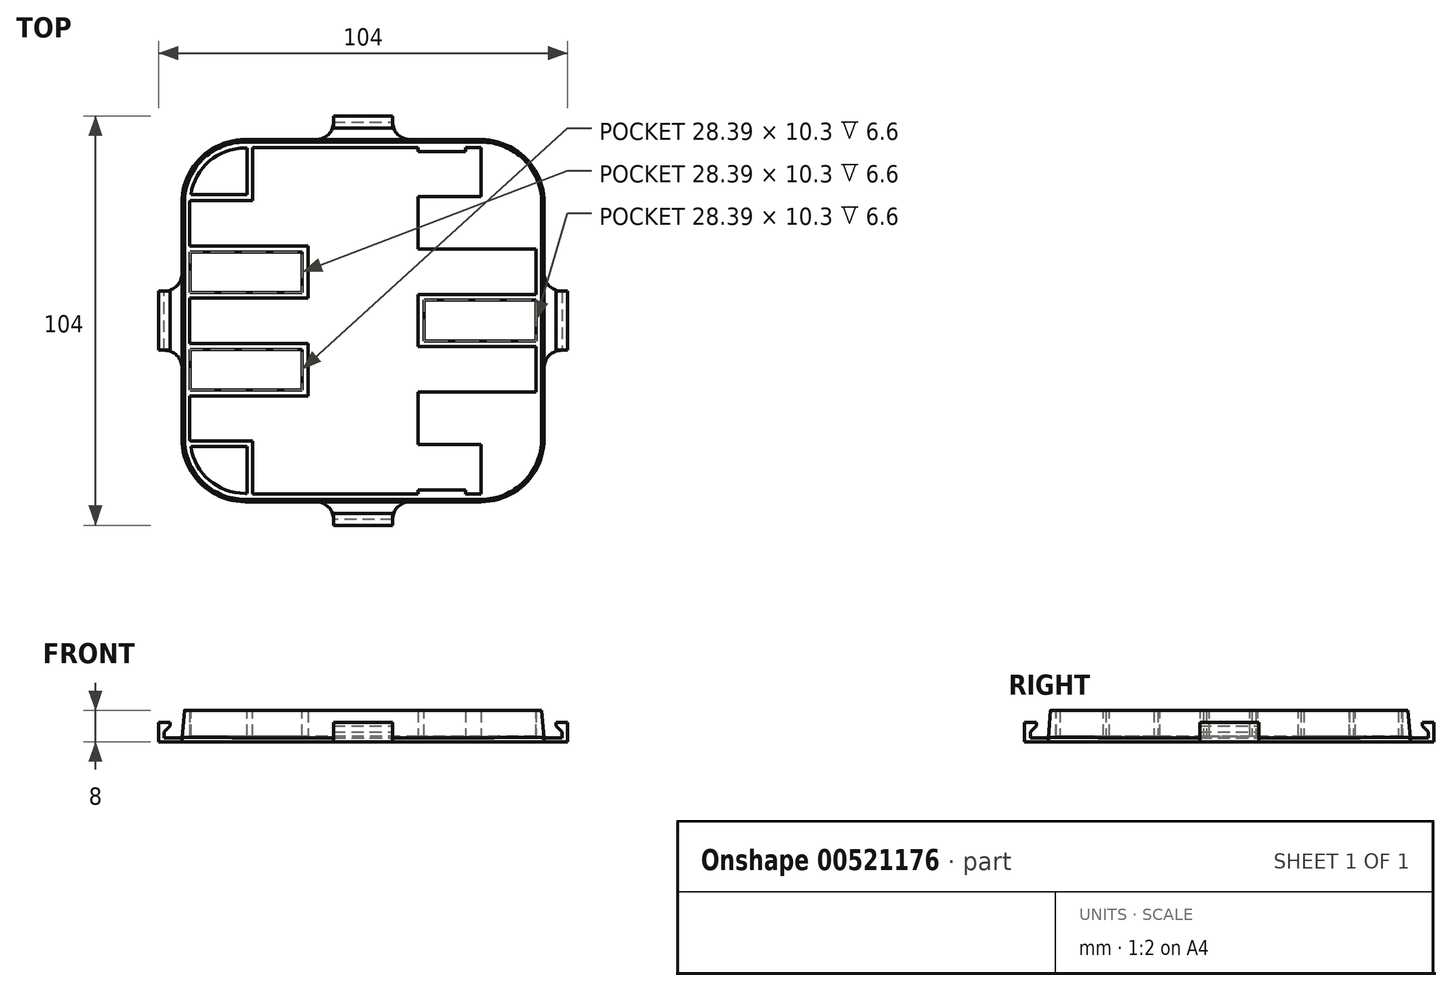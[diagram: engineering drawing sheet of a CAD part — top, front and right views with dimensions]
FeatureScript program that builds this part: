
annotation { "Feature Type Name" : "Feature", "Feature Type Description" : "" }
export const myFeature = defineFeature(function(context is Context, id is Id, definition is map)
    precondition{}
    {
        {
            var Q0;
            Q0=qCreatedBy(makeId("Top.planeOp"),FACE);
            var sketch = newSketch(context, id + "F0", { "sketchPlane" : qUnion([Q0])});
            skPoint(sketch, "E0.middle", {"position": v(0, 0) * mm});
            skPoint(sketch, "E1.visualSharp", {"position": v(40, 40) * mm});
            skArc(sketch, "E1.filletArc", {"start": v(52, 30) * mm, "mid": v(45.56, 45.56) * mm, "end": v(30, 52) * mm});
            skPoint(sketch, "E2.visualSharp", {"position": v(40, -40) * mm});
            skArc(sketch, "E2.filletArc", {"start": v(30, -52) * mm, "mid": v(45.56, -45.56) * mm, "end": v(52, -30) * mm});
            skPoint(sketch, "E3.visualSharp", {"position": v(-40, -40) * mm});
            skArc(sketch, "E3.filletArc", {"start": v(-52, -30) * mm, "mid": v(-45.56, -45.56) * mm, "end": v(-30, -52) * mm});
            skPoint(sketch, "E4.visualSharp", {"position": v(-40, 40) * mm});
            skArc(sketch, "E4.filletArc", {"start": v(-30, 52) * mm, "mid": v(-45.56, 45.56) * mm, "end": v(-52, 30) * mm});
            skLineSegment(sketch, "E5", {"start": v(52, 30) * mm, "end": v(52, 0) * mm});
            skLineSegment(sketch, "E6", {"start": v(52, 0) * mm, "end": v(52, -30) * mm});
            skLineSegment(sketch, "E7", {"start": v(30, 52) * mm, "end": v(0, 52) * mm});
            skLineSegment(sketch, "E8", {"start": v(0, 52) * mm, "end": v(-30, 52) * mm});
            skLineSegment(sketch, "E9", {"start": v(-52, 30) * mm, "end": v(-52, 0) * mm});
            skLineSegment(sketch, "E10", {"start": v(-52, 0) * mm, "end": v(-52, -30) * mm});
            skLineSegment(sketch, "E11", {"start": v(-30, -52) * mm, "end": v(0, -52) * mm});
            skLineSegment(sketch, "E12", {"start": v(0, -52) * mm, "end": v(30, -52) * mm});
            skSolve(sketch);
        }
        {
            var Q0;
            Q0=qCreatedBy(makeId("Front.planeOp"),FACE);
            var sketch = newSketch(context, id + "F1", { "sketchPlane" : qUnion([Q0])});
            skLineSegment(sketch, "E13", {"start": v(44, 0) * mm, "end": v(52, 0) * mm});
            skLineSegment(sketch, "E14", {"start": v(52, 0) * mm, "end": v(52, 1) * mm});
            skLineSegment(sketch, "E15", {"start": v(46, 1) * mm, "end": v(45.39, 8) * mm});
            skLineSegment(sketch, "E16", {"start": v(45.39, 8) * mm, "end": v(44, 8) * mm});
            skLineSegment(sketch, "E17", {"start": v(44, 8) * mm, "end": v(44, 0) * mm});
            skPoint(sketch, "E18.orphan", {"position": v(0, 8) * mm});
            skPoint(sketch, "E19.orphan", {"position": v(0, 0) * mm});
            skLineSegment(sketch, "E20", {"start": v(50.5, 1) * mm, "end": v(46, 1) * mm});
            skLineSegment(sketch, "E21", {"start": v(52, 1) * mm, "end": v(52, 5) * mm});
            skLineSegment(sketch, "E22", {"start": v(52, 5) * mm, "end": v(49, 5) * mm});
            skLineSegment(sketch, "E23", {"start": v(49, 5) * mm, "end": v(49, 4) * mm});
            skLineSegment(sketch, "E24", {"start": v(49, 4) * mm, "end": v(50.5, 2.5) * mm});
            skLineSegment(sketch, "E25", {"start": v(50.5, 2.5) * mm, "end": v(50.5, 1) * mm});
            skSolve(sketch);
        }
        {
            var Q0;
            Q0 = qSketchRegion(id + "F1", true);
            var Q1;
            Q1 = qConstructionFilter(qBodyType(qCreatedBy(id + "F0" ,EDGE), BodyType.WIRE), ConstructionObject.NO);
            sweep(context, id + "F2", {"profiles" : qUnion([Q0]), "path" : qUnion([Q1])});
        }
        {
            var Q0;
            Q0=qCreatedBy(makeId("Top.planeOp"),FACE);
            var sketch = newSketch(context, id + "F3", { "sketchPlane" : qUnion([Q0])});
            skLineSegment(sketch, "E26.0", {"start": v(-30, -44) * mm, "end": v(30, -44) * mm});
            skArc(sketch, "E27.0", {"start": v(-44, -30) * mm, "mid": v(-39.9, -39.9) * mm, "end": v(-30, -44) * mm});
            skLineSegment(sketch, "E28.0", {"start": v(-44, 30) * mm, "end": v(-44, -30) * mm});
            skArc(sketch, "E29.0", {"start": v(30, -44) * mm, "mid": v(39.9, -39.9) * mm, "end": v(44, -30) * mm});
            skLineSegment(sketch, "E30.0", {"start": v(44, -30) * mm, "end": v(44, 30) * mm});
            skArc(sketch, "E31.0", {"start": v(44, 30) * mm, "mid": v(39.9, 39.9) * mm, "end": v(30, 44) * mm});
            skLineSegment(sketch, "E32.0", {"start": v(30, 44) * mm, "end": v(-30, 44) * mm});
            skArc(sketch, "E33.0", {"start": v(-30, 44) * mm, "mid": v(-39.9, 39.9) * mm, "end": v(-44, 30) * mm});
            skSolve(sketch);
        }
        {
            var Q0;
            Q0 = qSketchRegion(id + "F3", true);
            extrude(context, id + "F4", {"entities" : qUnion([Q0]), "operationType" : NewBodyOperationType.ADD, "depth" : 1.4 * mm, "offsetDistance" : 25 * mm});
        }
        {
            var Q0;
            Q0=makeQuery(id+"F4.opExtrude","CAP_FACE",FACE,{"disambiguationData":[OSD([sQuery(id+"F3.wireOp",EDGE,"E26.0"),sQuery(id+"F3.wireOp",EDGE,"E27.0"),sQuery(id+"F3.wireOp",EDGE,"E28.0"),sQuery(id+"F3.wireOp",EDGE,"E29.0"),sQuery(id+"F3.wireOp",EDGE,"E30.0"),sQuery(id+"F3.wireOp",EDGE,"E31.0"),sQuery(id+"F3.wireOp",EDGE,"E32.0"),sQuery(id+"F3.wireOp",EDGE,"E33.0"),sQuery(id+"F3.wireOp",EDGE,"Zldg7baT-O6LS-5cXX-1kl8-0yIzSKLbcUxf")])],"isStart":false});
            var sketch = newSketch(context, id + "F5", { "sketchPlane" : qUnion([Q0])});
            skLineSegment(sketch, "E34.bottom", {"start": v(44, 31.5) * mm, "end": v(14, 31.5) * mm});
            skLineSegment(sketch, "E34.top", {"start": v(44, 18.2) * mm, "end": v(14, 18.2) * mm});
            skLineSegment(sketch, "E34.left", {"start": v(44, 31.5) * mm, "end": v(44, 18.2) * mm});
            skLineSegment(sketch, "E34.right", {"start": v(14, 31.5) * mm, "end": v(14, 18.2) * mm});
            skLineSegment(sketch, "E35.bottom", {"start": v(14, 44) * mm, "end": v(26, 44) * mm});
            skLineSegment(sketch, "E35.top", {"start": v(14, 43) * mm, "end": v(26, 43) * mm});
            skLineSegment(sketch, "E35.left", {"start": v(14, 44) * mm, "end": v(14, 43) * mm});
            skLineSegment(sketch, "E35.right", {"start": v(26, 44) * mm, "end": v(26, 43) * mm});
            skLineSegment(sketch, "E36.bottom", {"start": v(44, 6.7) * mm, "end": v(14, 6.7) * mm});
            skLineSegment(sketch, "E36.top", {"start": v(44, -6.6) * mm, "end": v(14, -6.6) * mm});
            skLineSegment(sketch, "E36.left", {"start": v(44, 6.7) * mm, "end": v(44, -6.6) * mm});
            skLineSegment(sketch, "E36.right", {"start": v(14, 6.7) * mm, "end": v(14, -6.6) * mm});
            skLineSegment(sketch, "E37.bottom", {"start": v(44, -18.1) * mm, "end": v(14, -18.1) * mm});
            skLineSegment(sketch, "E37.top", {"start": v(44, -31.4) * mm, "end": v(14, -31.4) * mm});
            skLineSegment(sketch, "E37.left", {"start": v(44, -18.1) * mm, "end": v(44, -31.4) * mm});
            skLineSegment(sketch, "E37.right", {"start": v(14, -18.1) * mm, "end": v(14, -31.4) * mm});
            skLineSegment(sketch, "E38.bottom", {"start": v(14, -44) * mm, "end": v(26, -44) * mm});
            skLineSegment(sketch, "E38.top", {"start": v(14, -43) * mm, "end": v(26, -43) * mm});
            skLineSegment(sketch, "E38.left", {"start": v(14, -44) * mm, "end": v(14, -43) * mm});
            skLineSegment(sketch, "E38.right", {"start": v(26, -44) * mm, "end": v(26, -43) * mm});
            skLineSegment(sketch, "E39.bottom", {"start": v(-44, 30.5) * mm, "end": v(-14, 30.5) * mm});
            skLineSegment(sketch, "E39.top", {"start": v(-30, 44) * mm, "end": v(-14, 44) * mm});
            skLineSegment(sketch, "E39.left", {"start": v(-44, 30) * mm, "end": v(-44, 30.5) * mm});
            skLineSegment(sketch, "E39.right", {"start": v(-14, 30.5) * mm, "end": v(-14, 44) * mm});
            skArc(sketch, "E40.0", {"start": v(-30, 44) * mm, "mid": v(-39.9, 39.9) * mm, "end": v(-44, 30) * mm});
            skLineSegment(sketch, "E41.bottom", {"start": v(-14, -44) * mm, "end": v(-30, -44) * mm});
            skLineSegment(sketch, "E41.top", {"start": v(-14, -30.5) * mm, "end": v(-44, -30.5) * mm});
            skLineSegment(sketch, "E41.left", {"start": v(-14, -44) * mm, "end": v(-14, -30.5) * mm});
            skLineSegment(sketch, "E41.right", {"start": v(-44, -30.5) * mm, "end": v(-44, -30) * mm});
            skArc(sketch, "E42.0", {"start": v(-44, -30) * mm, "mid": v(-39.9, -39.9) * mm, "end": v(-30, -44) * mm});
            skLineSegment(sketch, "E43.bottom", {"start": v(-44, 19) * mm, "end": v(-14, 19) * mm});
            skLineSegment(sketch, "E43.top", {"start": v(-44, 5.7) * mm, "end": v(-14, 5.7) * mm});
            skLineSegment(sketch, "E43.left", {"start": v(-44, 19) * mm, "end": v(-44, 5.7) * mm});
            skLineSegment(sketch, "E43.right", {"start": v(-14, 19) * mm, "end": v(-14, 5.7) * mm});
            skLineSegment(sketch, "E44.bottom", {"start": v(-44, -5.8) * mm, "end": v(-14, -5.8) * mm});
            skLineSegment(sketch, "E44.top", {"start": v(-44, -19.1) * mm, "end": v(-14, -19.1) * mm});
            skLineSegment(sketch, "E44.left", {"start": v(-44, -5.8) * mm, "end": v(-44, -19.1) * mm});
            skLineSegment(sketch, "E44.right", {"start": v(-14, -5.8) * mm, "end": v(-14, -19.1) * mm});
            skSolve(sketch);
        }
        {
            var Q0;
            Q0 = qSketchRegion(id + "F5", true);
            var Q1;
            Q1=makeQuery(id+"F2.opSweep","SWEPT_FACE",FACE,{"disambiguationData":[OSD([sQuery(id+"F0.wireOp",EDGE,"E5"),sQuery(id+"F1.wireOp",EDGE,"E16")])]});
            extrude(context, id + "F6", {"entities" : qUnion([Q0]), "operationType" : NewBodyOperationType.ADD, "endBound" : BoundingType.UP_TO_SURFACE, "depth" : 25 * mm, "endBoundEntityFace" : qUnion([Q1]), "offsetDistance" : 25 * mm});
        }
        {
            var Q0;
            Q0=makeQuery(id+"F4.opExtrude","CAP_FACE",FACE,{"disambiguationData":[OSD([sQuery(id+"F3.wireOp",EDGE,"E26.0"),sQuery(id+"F3.wireOp",EDGE,"E27.0"),sQuery(id+"F3.wireOp",EDGE,"E28.0"),sQuery(id+"F3.wireOp",EDGE,"E29.0"),sQuery(id+"F3.wireOp",EDGE,"E30.0"),sQuery(id+"F3.wireOp",EDGE,"E31.0"),sQuery(id+"F3.wireOp",EDGE,"E32.0"),sQuery(id+"F3.wireOp",EDGE,"E33.0")])],"isStart":false});
            var sketch = newSketch(context, id + "F7", { "sketchPlane" : qUnion([Q0])});
            skLineSegment(sketch, "E45", {"start": v(30, 44) * mm, "end": v(30, 31.5) * mm});
            skLineSegment(sketch, "E46", {"start": v(30, 31.5) * mm, "end": v(43.92, 31.5) * mm});
            skLineSegment(sketch, "E47", {"start": v(30, -44) * mm, "end": v(30, -31.4) * mm});
            skLineSegment(sketch, "E48", {"start": v(30, -31.4) * mm, "end": v(43.93, -31.4) * mm});
            skArc(sketch, "E49.0", {"start": v(30, -44) * mm, "mid": v(39.4, -40.38) * mm, "end": v(43.93, -31.4) * mm});
            skSolve(sketch);
        }
        {
            var Q0;
            Q0=makeQuery(id+"F7.imprint","IMPRINT",FACE,{"disambiguationData":[TD([[makeQuery(id+"F7.imprint","IMPRINT",EDGE,{"derivedFrom":sQuery(id+"F7.wireOp",EDGE,"E47")}),-1.0]])]});
            var Q1;
            Q1=makeQuery(id+"F7.imprint","IMPRINT",FACE,{"disambiguationData":[TD([[makeQuery(id+"F7.imprint","IMPRINT",EDGE,{"derivedFrom":sQuery(id+"F7.wireOp",EDGE,"E45")}),1.0]])]});
            var Q2;
            Q2=makeQuery(id+"F6.boolean.opBoolean","MERGE",FACE,{"derivedFrom":[makeQuery(id+"F2.opSweep","SWEPT_FACE",FACE,{"disambiguationData":[OSD([sQuery(id+"F0.wireOp",EDGE,"E5"),sQuery(id+"F1.wireOp",EDGE,"E16")])]}),makeQuery(id+"F6.opExtrude","CAP_FACE",FACE,{"disambiguationData":[OSD([sQuery(id+"F5.wireOp",EDGE,"E34.bottom"),sQuery(id+"F5.wireOp",EDGE,"E34.top"),sQuery(id+"F5.wireOp",EDGE,"E34.left"),sQuery(id+"F5.wireOp",EDGE,"E34.right")])],"isStart":false}),makeQuery(id+"F6.opExtrude","CAP_FACE",FACE,{"disambiguationData":[OSD([sQuery(id+"F5.wireOp",EDGE,"E35.bottom"),sQuery(id+"F5.wireOp",EDGE,"E35.top"),sQuery(id+"F5.wireOp",EDGE,"E35.left"),sQuery(id+"F5.wireOp",EDGE,"E35.right")])],"isStart":false}),makeQuery(id+"F6.opExtrude","CAP_FACE",FACE,{"disambiguationData":[OSD([sQuery(id+"F5.wireOp",EDGE,"E36.bottom"),sQuery(id+"F5.wireOp",EDGE,"E36.top"),sQuery(id+"F5.wireOp",EDGE,"E36.left"),sQuery(id+"F5.wireOp",EDGE,"E36.right")])],"isStart":false}),makeQuery(id+"F6.opExtrude","CAP_FACE",FACE,{"disambiguationData":[OSD([sQuery(id+"F5.wireOp",EDGE,"E37.bottom"),sQuery(id+"F5.wireOp",EDGE,"E37.top"),sQuery(id+"F5.wireOp",EDGE,"E37.left"),sQuery(id+"F5.wireOp",EDGE,"E37.right")])],"isStart":false}),makeQuery(id+"F6.opExtrude","CAP_FACE",FACE,{"disambiguationData":[OSD([sQuery(id+"F5.wireOp",EDGE,"E38.bottom"),sQuery(id+"F5.wireOp",EDGE,"E38.top"),sQuery(id+"F5.wireOp",EDGE,"E38.left"),sQuery(id+"F5.wireOp",EDGE,"E38.right")])],"isStart":false}),makeQuery(id+"F6.opExtrude","CAP_FACE",FACE,{"disambiguationData":[OSD([sQuery(id+"F5.wireOp",EDGE,"E39.bottom"),sQuery(id+"F5.wireOp",EDGE,"E39.top"),sQuery(id+"F5.wireOp",EDGE,"E39.right"),sQuery(id+"F5.wireOp",EDGE,"E40.0")])],"isStart":false}),makeQuery(id+"F6.opExtrude","CAP_FACE",FACE,{"disambiguationData":[OSD([sQuery(id+"F5.wireOp",EDGE,"E41.bottom"),sQuery(id+"F5.wireOp",EDGE,"E41.top"),sQuery(id+"F5.wireOp",EDGE,"E41.left"),sQuery(id+"F5.wireOp",EDGE,"E42.0")])],"isStart":false}),makeQuery(id+"F6.opExtrude","CAP_FACE",FACE,{"disambiguationData":[OSD([sQuery(id+"F5.wireOp",EDGE,"E43.bottom"),sQuery(id+"F5.wireOp",EDGE,"E43.top"),sQuery(id+"F5.wireOp",EDGE,"E43.left"),sQuery(id+"F5.wireOp",EDGE,"E43.right")])],"isStart":false}),makeQuery(id+"F6.opExtrude","CAP_FACE",FACE,{"disambiguationData":[OSD([sQuery(id+"F5.wireOp",EDGE,"E44.bottom"),sQuery(id+"F5.wireOp",EDGE,"E44.top"),sQuery(id+"F5.wireOp",EDGE,"E44.left"),sQuery(id+"F5.wireOp",EDGE,"E44.right")])],"isStart":false})]});
            extrude(context, id + "F8", {"entities" : qUnion([Q0, Q1]), "operationType" : NewBodyOperationType.ADD, "endBound" : BoundingType.UP_TO_SURFACE, "depth" : 25 * mm, "endBoundEntityFace" : qUnion([Q2]), "offsetDistance" : 25 * mm});
        }
        {
            var Q0;
            Q0=makeQuery(id+"F8.boolean.opBoolean","MERGE",FACE,{"derivedFrom":[makeQuery(id+"F6.boolean.opBoolean","MERGE",FACE,{"derivedFrom":[makeQuery(id+"F2.opSweep","SWEPT_FACE",FACE,{"disambiguationData":[OSD([sQuery(id+"F0.wireOp",EDGE,"E5"),sQuery(id+"F1.wireOp",EDGE,"E16")])]}),makeQuery(id+"F6.opExtrude","CAP_FACE",FACE,{"disambiguationData":[OSD([sQuery(id+"F5.wireOp",EDGE,"E34.bottom"),sQuery(id+"F5.wireOp",EDGE,"E34.top"),sQuery(id+"F5.wireOp",EDGE,"E34.left"),sQuery(id+"F5.wireOp",EDGE,"E34.right")])],"isStart":false}),makeQuery(id+"F6.opExtrude","CAP_FACE",FACE,{"disambiguationData":[OSD([sQuery(id+"F5.wireOp",EDGE,"E35.bottom"),sQuery(id+"F5.wireOp",EDGE,"E35.top"),sQuery(id+"F5.wireOp",EDGE,"E35.left"),sQuery(id+"F5.wireOp",EDGE,"E35.right")])],"isStart":false}),makeQuery(id+"F6.opExtrude","CAP_FACE",FACE,{"disambiguationData":[OSD([sQuery(id+"F5.wireOp",EDGE,"E36.bottom"),sQuery(id+"F5.wireOp",EDGE,"E36.top"),sQuery(id+"F5.wireOp",EDGE,"E36.left"),sQuery(id+"F5.wireOp",EDGE,"E36.right")])],"isStart":false}),makeQuery(id+"F6.opExtrude","CAP_FACE",FACE,{"disambiguationData":[OSD([sQuery(id+"F5.wireOp",EDGE,"E37.bottom"),sQuery(id+"F5.wireOp",EDGE,"E37.top"),sQuery(id+"F5.wireOp",EDGE,"E37.left"),sQuery(id+"F5.wireOp",EDGE,"E37.right")])],"isStart":false}),makeQuery(id+"F6.opExtrude","CAP_FACE",FACE,{"disambiguationData":[OSD([sQuery(id+"F5.wireOp",EDGE,"E38.bottom"),sQuery(id+"F5.wireOp",EDGE,"E38.top"),sQuery(id+"F5.wireOp",EDGE,"E38.left"),sQuery(id+"F5.wireOp",EDGE,"E38.right")])],"isStart":false}),makeQuery(id+"F6.opExtrude","CAP_FACE",FACE,{"disambiguationData":[OSD([sQuery(id+"F5.wireOp",EDGE,"E39.bottom"),sQuery(id+"F5.wireOp",EDGE,"E39.top"),sQuery(id+"F5.wireOp",EDGE,"E39.right"),sQuery(id+"F5.wireOp",EDGE,"E40.0")])],"isStart":false}),makeQuery(id+"F6.opExtrude","CAP_FACE",FACE,{"disambiguationData":[OSD([sQuery(id+"F5.wireOp",EDGE,"E41.bottom"),sQuery(id+"F5.wireOp",EDGE,"E41.top"),sQuery(id+"F5.wireOp",EDGE,"E41.left"),sQuery(id+"F5.wireOp",EDGE,"E42.0")])],"isStart":false}),makeQuery(id+"F6.opExtrude","CAP_FACE",FACE,{"disambiguationData":[OSD([sQuery(id+"F5.wireOp",EDGE,"E43.bottom"),sQuery(id+"F5.wireOp",EDGE,"E43.top"),sQuery(id+"F5.wireOp",EDGE,"E43.left"),sQuery(id+"F5.wireOp",EDGE,"E43.right")])],"isStart":false}),makeQuery(id+"F6.opExtrude","CAP_FACE",FACE,{"disambiguationData":[OSD([sQuery(id+"F5.wireOp",EDGE,"E44.bottom"),sQuery(id+"F5.wireOp",EDGE,"E44.top"),sQuery(id+"F5.wireOp",EDGE,"E44.left"),sQuery(id+"F5.wireOp",EDGE,"E44.right")])],"isStart":false})]}),makeQuery(id+"F8.opExtrude","CAP_FACE",FACE,{"disambiguationData":[OSD([sQuery(id+"F3.wireOp",EDGE,"E31.0"),sQuery(id+"F7.wireOp",EDGE,"E45"),sQuery(id+"F7.wireOp",EDGE,"E46")])],"isStart":false}),makeQuery(id+"F8.opExtrude","CAP_FACE",FACE,{"disambiguationData":[OSD([sQuery(id+"F7.wireOp",EDGE,"E47"),sQuery(id+"F7.wireOp",EDGE,"E48"),sQuery(id+"F7.wireOp",EDGE,"E49.0")])],"isStart":false})]});
            var sketch = newSketch(context, id + "F9", { "sketchPlane" : qUnion([Q0])});
            skLineSegment(sketch, "E50.bottom", {"start": v(-14, 44) * mm, "end": v(-28, 44) * mm});
            skLineSegment(sketch, "E50.top", {"start": v(-14, 30.5) * mm, "end": v(-28, 30.5) * mm});
            skLineSegment(sketch, "E50.left", {"start": v(-14, 44) * mm, "end": v(-14, 30.5) * mm});
            skLineSegment(sketch, "E50.right", {"start": v(-28, 44) * mm, "end": v(-28, 30.5) * mm});
            skLineSegment(sketch, "E51.bottom", {"start": v(-14, -44) * mm, "end": v(-28, -44) * mm});
            skLineSegment(sketch, "E51.top", {"start": v(-14, -30.5) * mm, "end": v(-28, -30.5) * mm});
            skLineSegment(sketch, "E51.left", {"start": v(-14, -44) * mm, "end": v(-14, -30.5) * mm});
            skLineSegment(sketch, "E51.right", {"start": v(-28, -44) * mm, "end": v(-28, -30.5) * mm});
            skSolve(sketch);
        }
        {
            var Q0;
            Q0=makeQuery(id+"F9.imprint","IMPRINT",FACE,{"disambiguationData":[TD([[makeQuery(id+"F9.imprint","IMPRINT",EDGE,{"derivedFrom":sQuery(id+"F9.wireOp",EDGE,"E50.bottom")}),1.0]])]});
            var Q1;
            Q1=makeQuery(id+"F9.imprint","IMPRINT",FACE,{"disambiguationData":[TD([[makeQuery(id+"F9.imprint","IMPRINT",EDGE,{"derivedFrom":sQuery(id+"F9.wireOp",EDGE,"E51.bottom")}),-1.0]])]});
            var Q2;
            Q2=makeQuery(id+"F4.opExtrude","CAP_FACE",FACE,{"disambiguationData":[OSD([sQuery(id+"F3.wireOp",EDGE,"E26.0"),sQuery(id+"F3.wireOp",EDGE,"E27.0"),sQuery(id+"F3.wireOp",EDGE,"E28.0"),sQuery(id+"F3.wireOp",EDGE,"E29.0"),sQuery(id+"F3.wireOp",EDGE,"E30.0"),sQuery(id+"F3.wireOp",EDGE,"E31.0"),sQuery(id+"F3.wireOp",EDGE,"E32.0"),sQuery(id+"F3.wireOp",EDGE,"E33.0")])],"isStart":false});
            extrude(context, id + "F10", {"entities" : qUnion([Q0, Q1]), "operationType" : NewBodyOperationType.REMOVE, "endBound" : BoundingType.UP_TO_SURFACE, "oppositeDirection" : true, "depth" : 25 * mm, "endBoundEntityFace" : qUnion([Q2]), "offsetDistance" : 25 * mm});
        }
        {
            var Q0;
            {var subQ0=sQuery(id+"F1.wireOp",EDGE,"E16");var subQ1=sQuery(id+"F0.wireOp",EDGE,"E5");Q0=makeQuery(id+"F6.boolean.opBoolean","MERGE",FACE,{"derivedFrom":[makeQuery(id+"F2.opSweep","SWEPT_FACE",FACE,{"disambiguationData":[OSD([subQ1,subQ0])]}),makeQuery(id+"F6.opExtrude","CAP_FACE",FACE,{"disambiguationData":[OSD([subQ1,subQ0]),OD(0.0)],"isStart":false}),makeQuery(id+"F6.opExtrude","CAP_FACE",FACE,{"disambiguationData":[OSD([subQ1,subQ0]),OD(1.0)],"isStart":false}),makeQuery(id+"F6.opExtrude","CAP_FACE",FACE,{"disambiguationData":[OSD([subQ1,subQ0]),OD(2.0)],"isStart":false}),makeQuery(id+"F6.opExtrude","CAP_FACE",FACE,{"disambiguationData":[OSD([subQ1,subQ0]),OD(3.0)],"isStart":false}),makeQuery(id+"F6.opExtrude","CAP_FACE",FACE,{"disambiguationData":[OSD([subQ1,subQ0]),OD(4.0)],"isStart":false}),makeQuery(id+"F6.opExtrude","CAP_FACE",FACE,{"disambiguationData":[OSD([subQ1,subQ0]),OD(5.0)],"isStart":false}),makeQuery(id+"F6.opExtrude","CAP_FACE",FACE,{"disambiguationData":[OSD([subQ1,subQ0]),OD(6.0)],"isStart":false}),makeQuery(id+"F6.opExtrude","CAP_FACE",FACE,{"disambiguationData":[OSD([subQ1,subQ0]),OD(7.0)],"isStart":false}),makeQuery(id+"F6.opExtrude","CAP_FACE",FACE,{"disambiguationData":[OSD([subQ1,subQ0]),OD(8.0)],"isStart":false})]});}
            var sketch = newSketch(context, id + "F11", { "sketchPlane" : qUnion([Q0])});
            skLineSegment(sketch, "E52.0", {"start": v(-29.5, 32) * mm, "end": v(-29.5, 43.89) * mm});
            skLineSegment(sketch, "E52.1", {"start": v(-43.74, 32) * mm, "end": v(-29.5, 32) * mm});
            skArc(sketch, "E53.1", {"start": v(-30, 43.89) * mm, "mid": v(-39.09, 40.5) * mm, "end": v(-43.74, 32) * mm});
            skLineSegment(sketch, "E53.2", {"start": v(-29.5, 43.89) * mm, "end": v(-30, 43.89) * mm});
            skLineSegment(sketch, "E54.0", {"start": v(-43.89, 7.2) * mm, "end": v(-15.5, 7.2) * mm});
            skLineSegment(sketch, "E54.1", {"start": v(-15.5, 17.5) * mm, "end": v(-15.5, 7.2) * mm});
            skLineSegment(sketch, "E54.2", {"start": v(-43.89, 17.5) * mm, "end": v(-15.5, 17.5) * mm});
            skLineSegment(sketch, "E55", {"start": v(-43.89, 17.5) * mm, "end": v(-43.89, 7.2) * mm});
            skLineSegment(sketch, "E56.0", {"start": v(-43.89, -17.6) * mm, "end": v(-15.5, -17.6) * mm});
            skLineSegment(sketch, "E56.1", {"start": v(-15.5, -7.3) * mm, "end": v(-15.5, -17.6) * mm});
            skLineSegment(sketch, "E56.2", {"start": v(-43.89, -7.3) * mm, "end": v(-15.5, -7.3) * mm});
            skLineSegment(sketch, "E57", {"start": v(-43.89, -7.3) * mm, "end": v(-43.89, -17.6) * mm});
            skLineSegment(sketch, "E58.0", {"start": v(43.89, 19.7) * mm, "end": v(15.5, 19.7) * mm});
            skLineSegment(sketch, "E58.1", {"start": v(15.5, 30) * mm, "end": v(15.5, 19.7) * mm});
            skLineSegment(sketch, "E58.2", {"start": v(31.5, 30) * mm, "end": v(15.5, 30) * mm});
            skLineSegment(sketch, "E59", {"start": v(43.89, 19.7) * mm, "end": v(43.89, 30) * mm});
            skLineSegment(sketch, "E60.0", {"start": v(43.89, -5.1) * mm, "end": v(15.5, -5.1) * mm});
            skLineSegment(sketch, "E60.1", {"start": v(15.5, 5.2) * mm, "end": v(15.5, -5.1) * mm});
            skLineSegment(sketch, "E60.2", {"start": v(43.89, 5.2) * mm, "end": v(15.5, 5.2) * mm});
            skLineSegment(sketch, "E61", {"start": v(43.89, -5.1) * mm, "end": v(43.89, 5.2) * mm});
            skLineSegment(sketch, "E62.1", {"start": v(15.5, -19.7) * mm, "end": v(15.5, -29.9) * mm});
            skLineSegment(sketch, "E63", {"start": v(43.89, -29.9) * mm, "end": v(43.89, -19.6) * mm});
            skArc(sketch, "E64.0", {"start": v(43.89, 30) * mm, "mid": v(39.82, 39.82) * mm, "end": v(30, 43.89) * mm});
            skLineSegment(sketch, "E65", {"start": v(31.5, 43.8) * mm, "end": v(31.5, 30) * mm});
            skLineSegment(sketch, "E66.MirrorCS", {"start": v(-43.74, -32) * mm, "end": v(-29.5, -32) * mm});
            skArc(sketch, "E67.MirrorCS", {"start": v(-30, -43.89) * mm, "mid": v(-39.09, -40.5) * mm, "end": v(-43.74, -32) * mm});
            skLineSegment(sketch, "E68.MirrorCS", {"start": v(-29.5, -32) * mm, "end": v(-29.5, -43.89) * mm});
            skLineSegment(sketch, "E69.MirrorCS", {"start": v(31.5, -43.8) * mm, "end": v(31.5, -30) * mm});
            skLineSegment(sketch, "E70.MirrorCS", {"start": v(31.5, -30) * mm, "end": v(15.5, -30) * mm});
            skLineSegment(sketch, "E71.MirrorCS", {"start": v(15.5, -30) * mm, "end": v(15.5, -19.7) * mm});
            skLineSegment(sketch, "E72.MirrorCS", {"start": v(43.89, -19.7) * mm, "end": v(15.5, -19.7) * mm});
            skLineSegment(sketch, "E73.MirrorCS", {"start": v(43.89, -19.7) * mm, "end": v(43.89, -30) * mm});
            skArc(sketch, "E74.MirrorCS", {"start": v(43.89, -30) * mm, "mid": v(39.82, -39.82) * mm, "end": v(30, -43.89) * mm});
            skLineSegment(sketch, "E75", {"start": v(-30, -43.89) * mm, "end": v(-29.5, -43.89) * mm});
            skSolve(sketch);
        }
        {
            var Q0;
            Q0=makeQuery(id+"F11.imprint","IMPRINT",FACE,{"disambiguationData":[TD([[makeQuery(id+"F11.imprint","IMPRINT",EDGE,{"derivedFrom":sQuery(id+"F11.wireOp",EDGE,"E52.0")}),1.0]])]});
            var Q1;
            Q1=makeQuery(id+"F11.imprint","IMPRINT",FACE,{"disambiguationData":[TD([[makeQuery(id+"F11.imprint","IMPRINT",EDGE,{"derivedFrom":sQuery(id+"F11.wireOp",EDGE,"E58.0")}),-1.0]])]});
            var Q2;
            Q2=makeQuery(id+"F11.imprint","IMPRINT",FACE,{"disambiguationData":[TD([[makeQuery(id+"F11.imprint","IMPRINT",EDGE,{"derivedFrom":sQuery(id+"F11.wireOp",EDGE,"E60.0")}),-1.0]])]});
            var Q3;
            {var subQ4=sQuery(id+"F11.wireOp",EDGE,"E69.MirrorCS");Q3=makeQuery(id+"F11.imprint","IMPRINT",FACE,{"disambiguationData":[TD([[makeQuery(id+"F11.imprint","IMPRINT",EDGE,{"derivedFrom":subQ4}),-1.0]])]});}
            var Q4;
            Q4=makeQuery(id+"F11.imprint","IMPRINT",FACE,{"disambiguationData":[TD([[makeQuery(id+"F11.imprint","IMPRINT",EDGE,{"derivedFrom":sQuery(id+"F11.wireOp",EDGE,"E54.0")}),1.0]])]});
            var Q5;
            Q5=makeQuery(id+"F11.imprint","IMPRINT",FACE,{"disambiguationData":[TD([[makeQuery(id+"F11.imprint","IMPRINT",EDGE,{"derivedFrom":sQuery(id+"F11.wireOp",EDGE,"E56.0")}),1.0]])]});
            var Q6;
            Q6=makeQuery(id+"F11.imprint","IMPRINT",FACE,{"disambiguationData":[TD([[makeQuery(id+"F11.imprint","IMPRINT",EDGE,{"derivedFrom":sQuery(id+"F11.wireOp",EDGE,"E66.MirrorCS")}),-1.0]])]});
            var Q7;
            Q7=makeQuery(id+"F10.boolean.opBoolean","MERGE",FACE,{"derivedFrom":[makeQuery(id+"F4.opExtrude","CAP_FACE",FACE,{"disambiguationData":[OSD([sQuery(id+"F3.wireOp",EDGE,"E26.0"),sQuery(id+"F3.wireOp",EDGE,"E27.0"),sQuery(id+"F3.wireOp",EDGE,"E28.0"),sQuery(id+"F3.wireOp",EDGE,"E29.0"),sQuery(id+"F3.wireOp",EDGE,"E30.0"),sQuery(id+"F3.wireOp",EDGE,"E31.0"),sQuery(id+"F3.wireOp",EDGE,"E32.0"),sQuery(id+"F3.wireOp",EDGE,"E33.0")])],"isStart":false})],"fromTools":[makeQuery(id+"F10.opExtrude","CAP_FACE",FACE,{"disambiguationData":[OSD([sQuery(id+"F9.wireOp",EDGE,"E50.bottom"),sQuery(id+"F9.wireOp",EDGE,"E50.top"),sQuery(id+"F9.wireOp",EDGE,"E50.left"),sQuery(id+"F9.wireOp",EDGE,"E50.right")])],"isStart":false}),makeQuery(id+"F10.opExtrude","CAP_FACE",FACE,{"disambiguationData":[OSD([sQuery(id+"F9.wireOp",EDGE,"E51.bottom"),sQuery(id+"F9.wireOp",EDGE,"E51.top"),sQuery(id+"F9.wireOp",EDGE,"E51.left"),sQuery(id+"F9.wireOp",EDGE,"E51.right")])],"isStart":false})]});
            extrude(context, id + "F12", {"entities" : qUnion([Q0, Q1, Q2, Q3, Q4, Q5, Q6]), "operationType" : NewBodyOperationType.REMOVE, "endBound" : BoundingType.UP_TO_SURFACE, "oppositeDirection" : true, "depth" : 6 * mm, "endBoundEntityFace" : qUnion([Q7]), "offsetDistance" : 25 * mm});
        }
        {
            var Q0;
            Q0=qCreatedBy(makeId("Top.planeOp"),FACE);
            var sketch = newSketch(context, id + "F13", { "sketchPlane" : qUnion([Q0])});
            skArc(sketch, "E76.0", {"start": v(46, 30) * mm, "mid": v(41.31, 41.31) * mm, "end": v(30, 46) * mm});
            skLineSegment(sketch, "E77", {"start": v(52, -7.5) * mm, "end": v(52, 7.5) * mm});
            skLineSegment(sketch, "E78", {"start": v(0, 0) * mm, "end": v(52, 0) * mm, "construction": true});
            skLineSegment(sketch, "E79", {"start": v(52, 7.5) * mm, "end": v(46, 7.5) * mm});
            skLineSegment(sketch, "E80", {"start": v(52, -7.5) * mm, "end": v(46, -7.5) * mm});
            skLineSegment(sketch, "E81.trimOffspring", {"start": v(46, 7.5) * mm, "end": v(46, 30) * mm});
            skLineSegment(sketch, "E82", {"start": v(46, -30) * mm, "end": v(46, -7.5) * mm});
            skLineSegment(sketch, "E83.1.0", {"start": v(30, 46) * mm, "end": v(7.5, 46) * mm});
            skLineSegment(sketch, "E83.1.1", {"start": v(-7.5, 46) * mm, "end": v(-30, 46) * mm});
            skLineSegment(sketch, "E83.1.2", {"start": v(0, 0) * mm, "end": v(0, 52) * mm, "construction": true});
            skLineSegment(sketch, "E83.1.3", {"start": v(7.5, 52) * mm, "end": v(-7.5, 52) * mm});
            skArc(sketch, "E83.1.4", {"start": v(-30, 46) * mm, "mid": v(-41.31, 41.31) * mm, "end": v(-46, 30) * mm});
            skLineSegment(sketch, "E83.1.5", {"start": v(7.5, 52) * mm, "end": v(7.5, 46) * mm});
            skLineSegment(sketch, "E83.1.6", {"start": v(-7.5, 52) * mm, "end": v(-7.5, 46) * mm});
            skLineSegment(sketch, "E83.2.0", {"start": v(-46, 30) * mm, "end": v(-46, 7.5) * mm});
            skLineSegment(sketch, "E83.2.1", {"start": v(-46, -7.5) * mm, "end": v(-46, -30) * mm});
            skLineSegment(sketch, "E83.2.2", {"start": v(0, 0) * mm, "end": v(-52, 0) * mm, "construction": true});
            skLineSegment(sketch, "E83.2.3", {"start": v(-52, 7.5) * mm, "end": v(-52, -7.5) * mm});
            skArc(sketch, "E83.2.4", {"start": v(-46, -30) * mm, "mid": v(-41.31, -41.31) * mm, "end": v(-30, -46) * mm});
            skLineSegment(sketch, "E83.2.5", {"start": v(-52, 7.5) * mm, "end": v(-46, 7.5) * mm});
            skLineSegment(sketch, "E83.2.6", {"start": v(-52, -7.5) * mm, "end": v(-46, -7.5) * mm});
            skLineSegment(sketch, "E83.3.0", {"start": v(-30, -46) * mm, "end": v(-7.5, -46) * mm});
            skLineSegment(sketch, "E83.3.1", {"start": v(7.5, -46) * mm, "end": v(30, -46) * mm});
            skLineSegment(sketch, "E83.3.2", {"start": v(0, 0) * mm, "end": v(0, -52) * mm, "construction": true});
            skLineSegment(sketch, "E83.3.3", {"start": v(-7.5, -52) * mm, "end": v(7.5, -52) * mm});
            skArc(sketch, "E83.3.4", {"start": v(30, -46) * mm, "mid": v(41.31, -41.31) * mm, "end": v(46, -30) * mm});
            skLineSegment(sketch, "E83.3.5", {"start": v(-7.5, -52) * mm, "end": v(-7.5, -46) * mm});
            skLineSegment(sketch, "E83.3.6", {"start": v(7.5, -52) * mm, "end": v(7.5, -46) * mm});
            skPoint(sketch, "E83.center", {"position": v(0, 0) * mm});
            skLineSegment(sketch, "E84.0.0", {"start": v(52, 30) * mm, "end": v(52, -30) * mm});
            skArc(sketch, "E84.0.1", {"start": v(52, -30) * mm, "mid": v(45.56, -45.56) * mm, "end": v(30, -52) * mm});
            skLineSegment(sketch, "E84.0.2", {"start": v(30, -52) * mm, "end": v(-30, -52) * mm});
            skArc(sketch, "E84.0.3", {"start": v(-30, -52) * mm, "mid": v(-45.56, -45.56) * mm, "end": v(-52, -30) * mm});
            skLineSegment(sketch, "E84.0.4", {"start": v(-52, -30) * mm, "end": v(-52, 30) * mm});
            skArc(sketch, "E84.0.5", {"start": v(-52, 30) * mm, "mid": v(-45.56, 45.56) * mm, "end": v(-30, 52) * mm});
            skLineSegment(sketch, "E84.0.6", {"start": v(-30, 52) * mm, "end": v(30, 52) * mm});
            skArc(sketch, "E84.0.7", {"start": v(30, 52) * mm, "mid": v(45.56, 45.56) * mm, "end": v(52, 30) * mm});
            skSolve(sketch);
        }
        {
            var Q0;
            {var subQ0=sQuery(id+"F13.wireOp",EDGE,"E80");Q0=makeQuery(id+"F13.imprint","IMPRINT",FACE,{"disambiguationData":[TD([[makeQuery(id+"F13.imprint","IMPRINT",EDGE,{"derivedFrom":subQ0}),1.0]])]});}
            var Q1;
            Q1=makeQuery(id+"F13.imprint","IMPRINT",FACE,{"disambiguationData":[TD([[makeQuery(id+"F13.imprint","IMPRINT",EDGE,{"derivedFrom":sQuery(id+"F13.wireOp",EDGE,"E83.2.1")}),-1.0]])]});
            var Q2;
            Q2=makeQuery(id+"F13.imprint","IMPRINT",FACE,{"disambiguationData":[TD([[makeQuery(id+"F13.imprint","IMPRINT",EDGE,{"derivedFrom":sQuery(id+"F13.wireOp",EDGE,"E83.1.1")}),-1.0]])]});
            var Q3;
            Q3=makeQuery(id+"F13.imprint","IMPRINT",FACE,{"disambiguationData":[TD([[makeQuery(id+"F13.imprint","IMPRINT",EDGE,{"derivedFrom":sQuery(id+"F13.wireOp",EDGE,"E76.0")}),-1.0]])]});
            extrude(context, id + "F14", {"entities" : qUnion([Q0, Q1, Q2, Q3]), "operationType" : NewBodyOperationType.REMOVE, "endBound" : BoundingType.UP_TO_NEXT, "depth" : 25 * mm, "offsetDistance" : 25 * mm});
        }
        {
            var Q0;
            Q0=makeQuery(id+"F14.boolean.opBoolean","COPY",EDGE,{"derivedFrom":makeQuery(id+"F14.opExtrude","SWEPT_EDGE",EDGE,{"disambiguationData":[OSD([sQuery(id+"F13.wireOp",EDGE,"E83.2.0"),sQuery(id+"F13.wireOp",EDGE,"E83.2.5")])]})});
            var Q1;
            Q1=makeQuery(id+"F14.boolean.opBoolean","COPY",EDGE,{"derivedFrom":makeQuery(id+"F14.opExtrude","SWEPT_EDGE",EDGE,{"disambiguationData":[OSD([sQuery(id+"F13.wireOp",EDGE,"E83.1.1"),sQuery(id+"F13.wireOp",EDGE,"E83.1.6")])]})});
            var Q2;
            Q2=makeQuery(id+"F14.boolean.opBoolean","COPY",EDGE,{"derivedFrom":makeQuery(id+"F14.opExtrude","SWEPT_EDGE",EDGE,{"disambiguationData":[OSD([sQuery(id+"F13.wireOp",EDGE,"E83.1.0"),sQuery(id+"F13.wireOp",EDGE,"E83.1.5")])]})});
            var Q3;
            Q3=makeQuery(id+"F14.boolean.opBoolean","COPY",EDGE,{"derivedFrom":makeQuery(id+"F14.opExtrude","SWEPT_EDGE",EDGE,{"disambiguationData":[OSD([sQuery(id+"F13.wireOp",EDGE,"E83.3.1"),sQuery(id+"F13.wireOp",EDGE,"E83.3.6")])]})});
            var Q4;
            Q4=makeQuery(id+"F14.boolean.opBoolean","COPY",EDGE,{"derivedFrom":makeQuery(id+"F14.opExtrude","SWEPT_EDGE",EDGE,{"disambiguationData":[OSD([sQuery(id+"F13.wireOp",EDGE,"E83.3.0"),sQuery(id+"F13.wireOp",EDGE,"E83.3.5")])]})});
            var Q5;
            Q5=makeQuery(id+"F14.boolean.opBoolean","COPY",EDGE,{"derivedFrom":makeQuery(id+"F14.opExtrude","SWEPT_EDGE",EDGE,{"disambiguationData":[OSD([sQuery(id+"F13.wireOp",EDGE,"E83.2.1"),sQuery(id+"F13.wireOp",EDGE,"E83.2.6")])]})});
            var Q6;
            Q6=makeQuery(id+"F14.boolean.opBoolean","COPY",EDGE,{"derivedFrom":makeQuery(id+"F14.opExtrude","SWEPT_EDGE",EDGE,{"disambiguationData":[OSD([sQuery(id+"F13.wireOp",EDGE,"E80"),sQuery(id+"F13.wireOp",EDGE,"E82")])]})});
            var Q7;
            Q7=makeQuery(id+"F14.boolean.opBoolean","COPY",EDGE,{"derivedFrom":makeQuery(id+"F14.opExtrude","SWEPT_EDGE",EDGE,{"disambiguationData":[OSD([sQuery(id+"F13.wireOp",EDGE,"E79"),sQuery(id+"F13.wireOp",EDGE,"E81.trimOffspring")])]})});
            fillet(context, id + "F15", {"entities" : qUnion([Q0, Q1, Q2, Q3, Q4, Q5, Q6, Q7]), "radius" : 4.5 * mm, "tangentPropagation" : true, "allowEdgeOverflow" : false});
        }
    });
